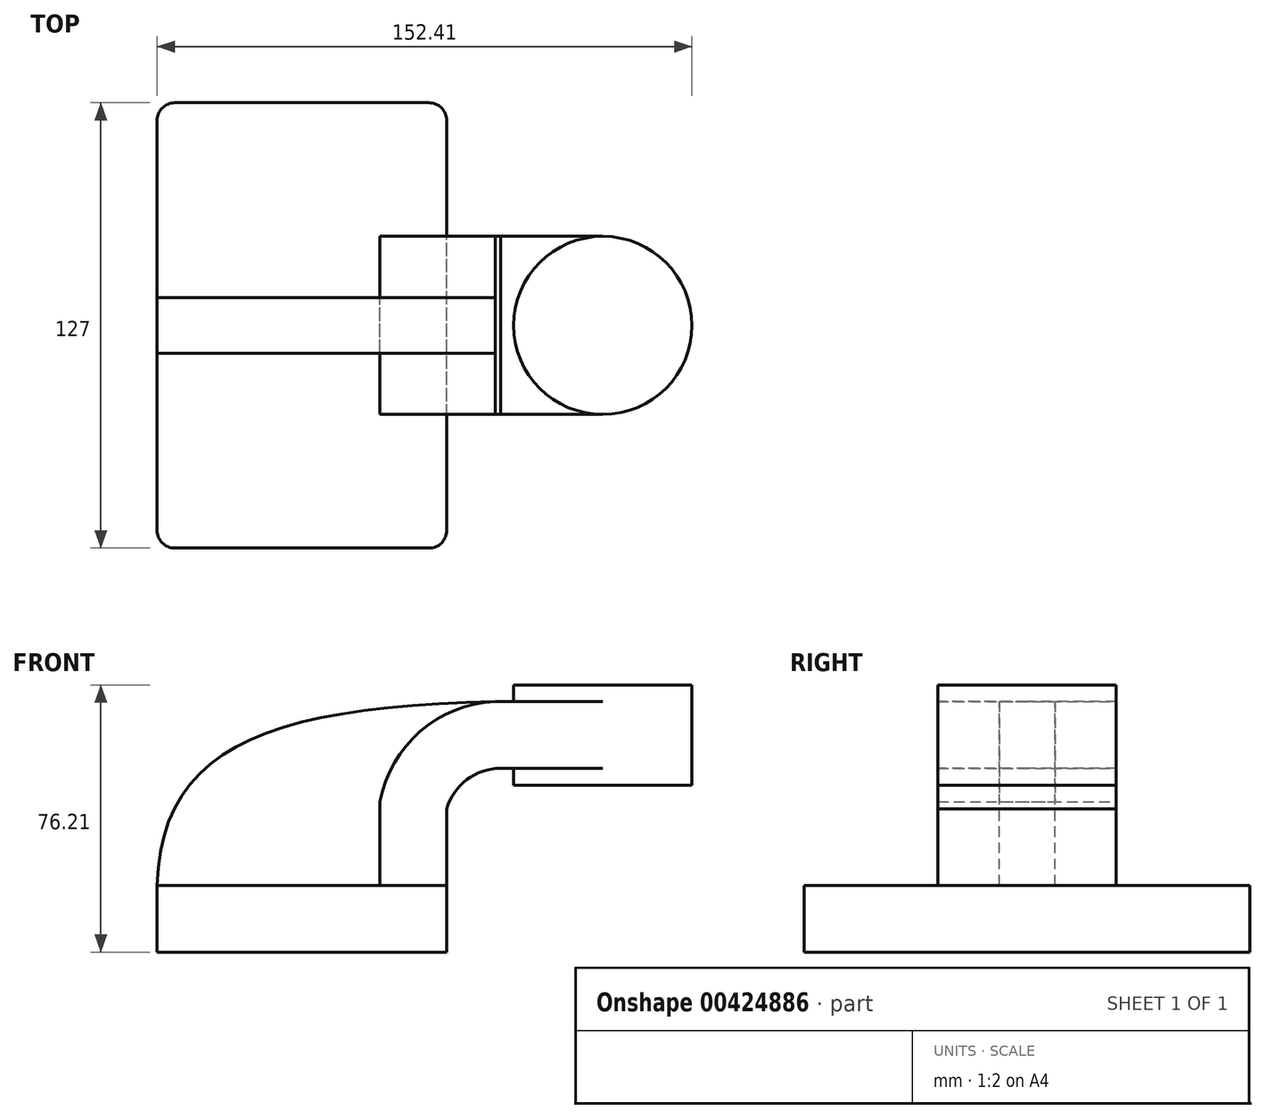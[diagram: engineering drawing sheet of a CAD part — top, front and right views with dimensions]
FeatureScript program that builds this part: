
annotation { "Feature Type Name" : "Feature", "Feature Type Description" : "" }
export const myFeature = defineFeature(function(context is Context, id is Id, definition is map)
    precondition{}
    {
        {
            var Q0;
            Q0=qCreatedBy(makeId("Front.planeOp"),FACE);
            var sketch = newSketch(context, id + "F0", { "sketchPlane" : qUnion([Q0])});
            skLineSegment(sketch, "E0.bottom", {"start": v(-41.28, -9.52) * mm, "end": v(41.28, -9.52) * mm});
            skLineSegment(sketch, "E0.top", {"start": v(-41.28, 9.53) * mm, "end": v(41.28, 9.53) * mm});
            skLineSegment(sketch, "E0.left", {"start": v(-41.28, -9.52) * mm, "end": v(-41.28, 9.53) * mm});
            skLineSegment(sketch, "E0.right", {"start": v(41.28, -9.52) * mm, "end": v(41.28, 9.53) * mm});
            skPoint(sketch, "E0.middle", {"position": v(0, 0) * mm});
            skLineSegment(sketch, "E1.bottom", {"start": v(60.33, 38.1) * mm, "end": v(111.12, 38.1) * mm});
            skLineSegment(sketch, "E1.top", {"start": v(60.33, 66.68) * mm, "end": v(111.12, 66.68) * mm});
            skLineSegment(sketch, "E1.left", {"start": v(60.33, 38.1) * mm, "end": v(60.33, 66.68) * mm});
            skLineSegment(sketch, "E1.right", {"start": v(111.12, 38.1) * mm, "end": v(111.12, 66.68) * mm});
            skPoint(sketch, "E1.middle", {"position": v(85.72, 52.39) * mm});
            skLineSegment(sketch, "E2", {"start": v(41.28, 9.53) * mm, "end": v(41.28, 31.3) * mm});
            skArc(sketch, "E3", {"start": v(41.28, 31.3) * mm, "mid": v(46.97, 39.65) * mm, "end": v(56.56, 42.88) * mm});
            skLineSegment(sketch, "E4", {"start": v(56.56, 42.88) * mm, "end": v(85.72, 42.88) * mm});
            skLineSegment(sketch, "E5.0", {"start": v(56.56, 61.93) * mm, "end": v(85.72, 61.93) * mm});
            skArc(sketch, "E5.1", {"start": v(22.22, 33.4) * mm, "mid": v(34.24, 53.86) * mm, "end": v(56.56, 61.93) * mm});
            skLineSegment(sketch, "E5.2", {"start": v(22.22, 9.53) * mm, "end": v(22.22, 33.4) * mm});
            skLineSegment(sketch, "E6", {"start": v(85.72, 38.1) * mm, "end": v(85.72, 66.68) * mm});
            skFitSpline(sketch, "E7", {"points": [v(-41.28, 9.53) * mm, v(56.56, 61.93) * mm], "startDerivative": vector(3.67, 119.87) * mm, "endDerivative": vector(196.6, 4.03) * mm});
            skSolve(sketch);
        }
        {
            var Q0;
            Q0=makeQuery(id+"F0.imprint","IMPRINT",FACE,{"disambiguationData":[TD([[makeQuery(id+"F0.imprint","IMPRINT",EDGE,{"derivedFrom":sQuery(id+"F0.wireOp",EDGE,"E0.bottom")}),1.0]])]});
            extrude(context, id + "F1", {"entities" : qUnion([Q0]), "endBound" : BoundingType.SYMMETRIC, "depth" : 127 * mm});
        }
        {
            var Q0;
            {var subQ1=sQuery(id+"F0.wireOp",EDGE,"E2");Q0=makeQuery(id+"F0.imprint","IMPRINT",FACE,{"disambiguationData":[TD([[makeQuery(id+"F0.imprint","IMPRINT",EDGE,{"derivedFrom":subQ1}),1.0]])]});}
            var Q1;
            {var subQ0=sQuery(id+"F0.wireOp",EDGE,"E4");var subQ1=sQuery(id+"F0.wireOp",EDGE,"E1.left");var subQ2=makeQuery(id+"F0.imprint","INTERSECT",VERTEX,{"derivedFrom":[subQ1,subQ0]});Q1=makeQuery(id+"F0.imprint","IMPRINT",FACE,{"disambiguationData":[TD([[makeQuery(id+"F0.imprint","IMPRINT",EDGE,{"disambiguationData":[TD([[subQ2,-1.0]])],"derivedFrom":subQ1}),-1.0]])]});}
            extrude(context, id + "F2", {"entities" : qUnion([Q0, Q1]), "endBound" : BoundingType.SYMMETRIC, "depth" : 50.8 * mm});
        }
        {
            var Q0;
            {var subQ3=sQuery(id+"F0.wireOp",EDGE,"E5.2");Q0=makeQuery(id+"F0.imprint","IMPRINT",FACE,{"disambiguationData":[TD([[makeQuery(id+"F0.imprint","IMPRINT",EDGE,{"derivedFrom":subQ3}),1.0]])]});}
            extrude(context, id + "F3", {"entities" : qUnion([Q0]), "endBound" : BoundingType.SYMMETRIC, "depth" : 15.88 * mm});
        }
        {
            var Q0;
            {var subQ4=sQuery(id+"F0.wireOp",EDGE,"E1.right");Q0=makeQuery(id+"F0.imprint","IMPRINT",FACE,{"disambiguationData":[TD([[makeQuery(id+"F0.imprint","IMPRINT",EDGE,{"derivedFrom":subQ4}),1.0]])]});}
            var Q1;
            Q1=sQuery(id+"F0.wireOp",EDGE,"E6");
            revolve(context, id + "F4", {"operationType" : NewBodyOperationType.ADD, "entities" : qUnion([Q0]), "axis" : qUnion([Q1]), "revolveType" : RevolveType.FULL});
        }
        {
            var Q0;
            Q0=makeQuery(id+"F1.opExtrude","CAP_EDGE",EDGE,{"disambiguationData":[OSD([sQuery(id+"F0.wireOp",EDGE,"E0.left")])],"isStart":false});
            var Q1;
            Q1=makeQuery(id+"F1.opExtrude","CAP_EDGE",EDGE,{"disambiguationData":[OSD([sQuery(id+"F0.wireOp",EDGE,"E0.right")])],"isStart":false});
            var Q2;
            Q2=makeQuery(id+"F1.opExtrude","CAP_EDGE",EDGE,{"disambiguationData":[OSD([sQuery(id+"F0.wireOp",EDGE,"E0.right")])],"isStart":true});
            var Q3;
            Q3=makeQuery(id+"F1.opExtrude","CAP_EDGE",EDGE,{"disambiguationData":[OSD([sQuery(id+"F0.wireOp",EDGE,"E0.left")])],"isStart":true});
            fillet(context, id + "F5", {"entities" : qUnion([Q0, Q1, Q2, Q3]), "radius" : 5.08 * mm, "tangentPropagation" : true, "allowEdgeOverflow" : false});
        }
    });
